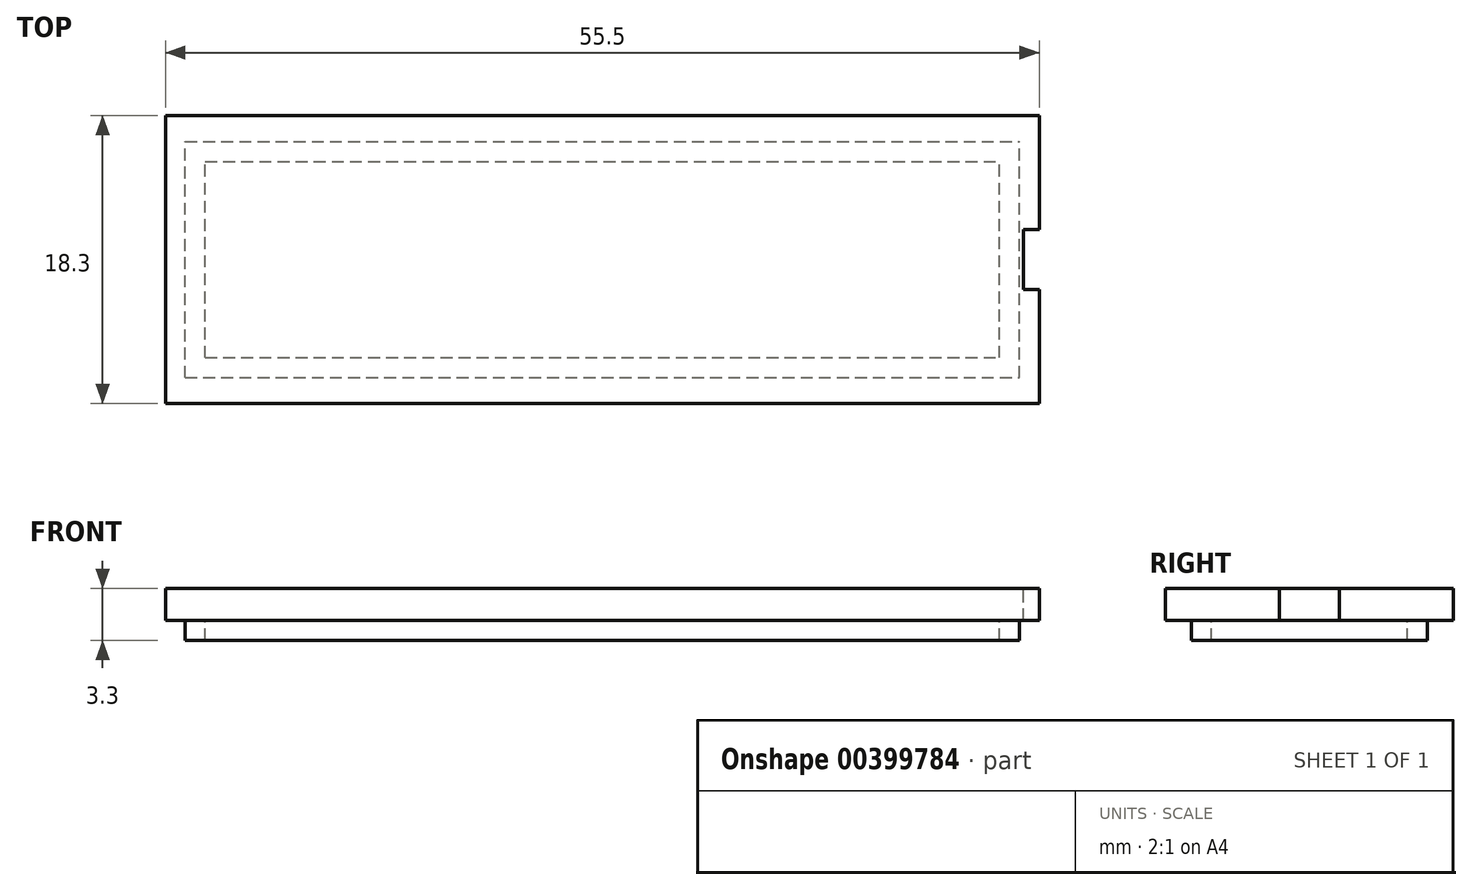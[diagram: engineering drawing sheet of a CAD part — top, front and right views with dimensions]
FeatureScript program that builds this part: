
annotation { "Feature Type Name" : "Feature", "Feature Type Description" : "" }
export const myFeature = defineFeature(function(context is Context, id is Id, definition is map)
    precondition{}
    {
        {
            var Q0;
            Q0=qCreatedBy(makeId("Top.planeOp"),FACE);
            var sketch = newSketch(context, id + "F0", { "sketchPlane" : qUnion([Q0])});
            skLineSegment(sketch, "E0.bottom", {"start": v(-9.64, 6.68) * mm, "end": v(45.86, 6.68) * mm});
            skLineSegment(sketch, "E0.top", {"start": v(-9.64, -11.62) * mm, "end": v(45.86, -11.62) * mm});
            skLineSegment(sketch, "E0.left", {"start": v(-9.64, 6.68) * mm, "end": v(-9.64, -11.62) * mm});
            skLineSegment(sketch, "E0.right", {"start": v(45.86, 6.68) * mm, "end": v(45.86, -11.62) * mm});
            skSolve(sketch);
        }
        {
            var Q0;
            Q0=makeQuery(id+"F0.imprint","IMPRINT",FACE,{"disambiguationData":[TD([[makeQuery(id+"F0.imprint","IMPRINT",EDGE,{"derivedFrom":sQuery(id+"F0.wireOp",EDGE,"E0.bottom")}),-1.0]])]});
            extrude(context, id + "F1", {"entities" : qUnion([Q0]), "depth" : 2.03 * mm});
        }
        {
            var Q0;
            Q0=makeQuery(id+"F1.opExtrude","CAP_FACE",FACE,{"disambiguationData":[OSD([sQuery(id+"F0.wireOp",EDGE,"E0.bottom"),sQuery(id+"F0.wireOp",EDGE,"E0.top"),sQuery(id+"F0.wireOp",EDGE,"E0.left"),sQuery(id+"F0.wireOp",EDGE,"E0.right")])],"isStart":false});
            var sketch = newSketch(context, id + "F2", { "sketchPlane" : qUnion([Q0])});
            skLineSegment(sketch, "E1.bottom", {"start": v(44.84, -0.57) * mm, "end": v(45.86, -0.57) * mm});
            skLineSegment(sketch, "E1.top", {"start": v(44.84, -4.38) * mm, "end": v(45.86, -4.38) * mm});
            skLineSegment(sketch, "E1.left", {"start": v(44.84, -0.57) * mm, "end": v(44.84, -4.38) * mm});
            skLineSegment(sketch, "E1.right", {"start": v(45.86, -0.57) * mm, "end": v(45.86, -4.38) * mm});
            skPoint(sketch, "E2", {"position": v(45.86, -2.47) * mm});
            skSolve(sketch);
        }
        {
            var Q0;
            Q0=makeQuery(id+"F2.imprint","IMPRINT",FACE,{"disambiguationData":[TD([[makeQuery(id+"F2.imprint","IMPRINT",EDGE,{"derivedFrom":sQuery(id+"F2.wireOp",EDGE,"E1.bottom")}),-1.0]])]});
            extrude(context, id + "F3", {"entities" : qUnion([Q0]), "operationType" : NewBodyOperationType.REMOVE, "oppositeDirection" : true, "depth" : 2.3 * mm});
        }
        {
            var Q0;
            Q0=makeQuery(id+"F1.opExtrude","CAP_FACE",FACE,{"disambiguationData":[OSD([sQuery(id+"F0.wireOp",EDGE,"E0.bottom"),sQuery(id+"F0.wireOp",EDGE,"E0.top"),sQuery(id+"F0.wireOp",EDGE,"E0.left"),sQuery(id+"F0.wireOp",EDGE,"E0.right")])],"isStart":true});
            var sketch = newSketch(context, id + "F4", { "sketchPlane" : qUnion([Q0])});
            skLineSegment(sketch, "E3.bottom", {"start": v(-8.4, 9.97) * mm, "end": v(44.6, 9.97) * mm});
            skLineSegment(sketch, "E3.top", {"start": v(-8.4, -5.03) * mm, "end": v(44.6, -5.03) * mm});
            skLineSegment(sketch, "E3.left", {"start": v(-8.4, 9.97) * mm, "end": v(-8.4, -5.03) * mm});
            skLineSegment(sketch, "E3.right", {"start": v(44.6, 9.97) * mm, "end": v(44.6, -5.03) * mm});
            skLineSegment(sketch, "E4.0", {"start": v(-7.12, 8.7) * mm, "end": v(-7.12, -3.76) * mm});
            skLineSegment(sketch, "E4.1", {"start": v(-7.12, 8.7) * mm, "end": v(43.34, 8.7) * mm});
            skLineSegment(sketch, "E4.2", {"start": v(43.34, 8.7) * mm, "end": v(43.34, -3.76) * mm});
            skLineSegment(sketch, "E4.3", {"start": v(-7.12, -3.76) * mm, "end": v(43.34, -3.76) * mm});
            skSolve(sketch);
        }
        {
            var Q0;
            {var subQ3=sQuery(id+"F4.wireOp",EDGE,"E3.bottom");Q0=makeQuery(id+"F4.imprint","IMPRINT",FACE,{"disambiguationData":[TD([[makeQuery(id+"F4.imprint","IMPRINT",EDGE,{"derivedFrom":subQ3}),-1.0]])]});}
            extrude(context, id + "F5", {"entities" : qUnion([Q0]), "operationType" : NewBodyOperationType.ADD, "depth" : 1.27 * mm});
        }
    });
